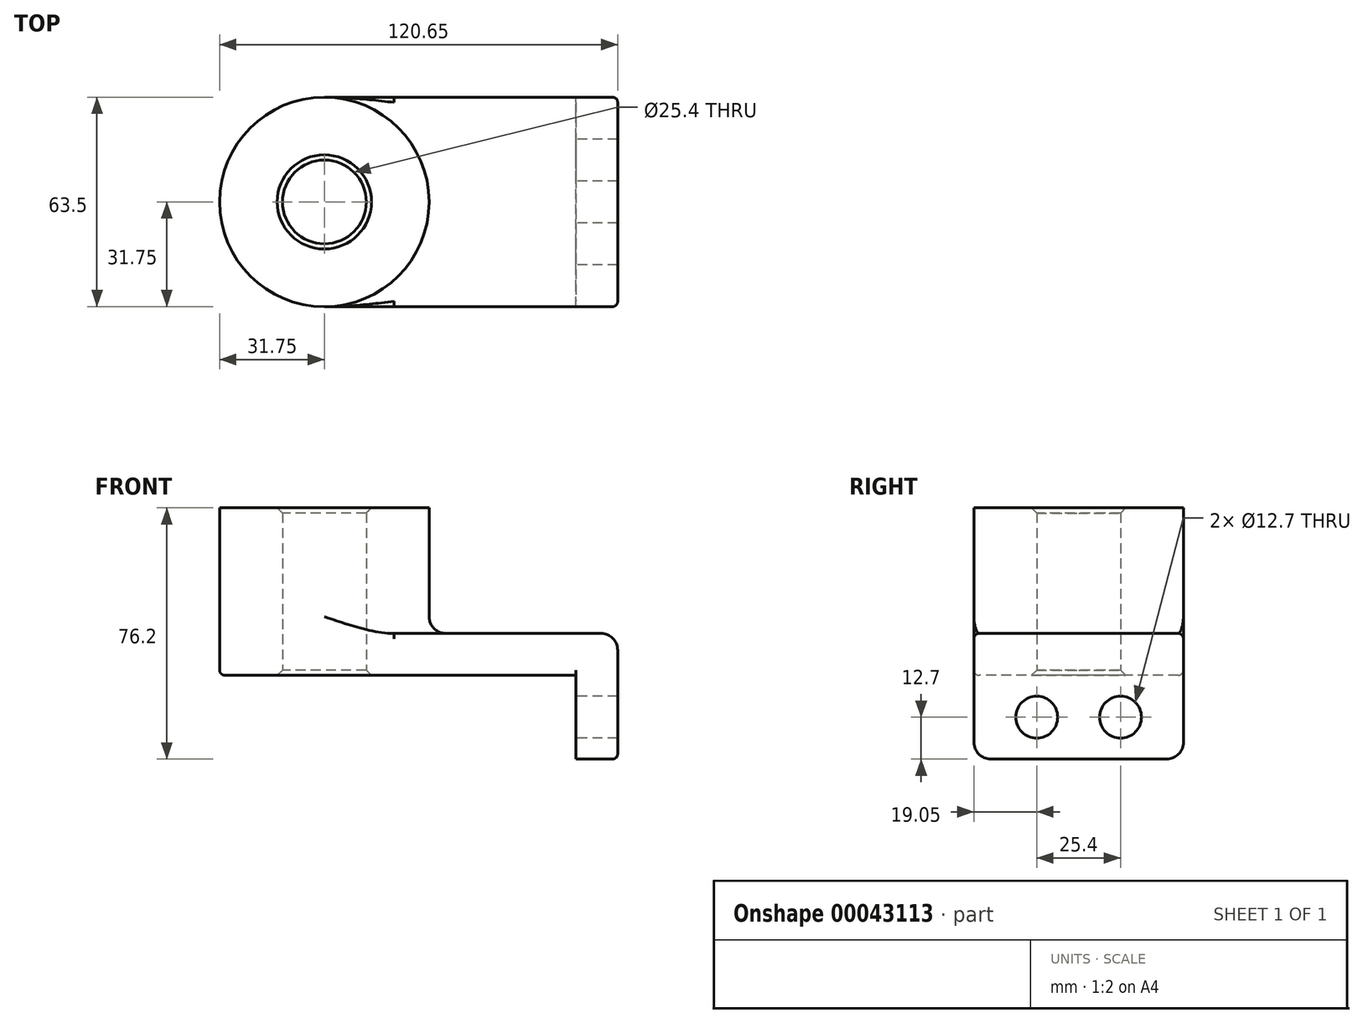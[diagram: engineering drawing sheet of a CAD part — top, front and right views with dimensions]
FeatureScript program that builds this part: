
annotation { "Feature Type Name" : "Feature", "Feature Type Description" : "" }
export const myFeature = defineFeature(function(context is Context, id is Id, definition is map)
    precondition{}
    {
        {
            var Q0;
            Q0=qCreatedBy(makeId("Top.planeOp"),FACE);
            var sketch = newSketch(context, id + "F0", { "sketchPlane" : qUnion([Q0])});
            skLineSegment(sketch, "E0.rect.bottom", {"start": v(-38.1, 31.75) * mm, "end": v(38.1, 31.75) * mm});
            skLineSegment(sketch, "E0.rect.top", {"start": v(-38.1, -31.75) * mm, "end": v(38.1, -31.75) * mm});
            skLineSegment(sketch, "E0.rect.left", {"start": v(-38.1, 31.75) * mm, "end": v(-38.1, -31.75) * mm});
            skLineSegment(sketch, "E0.rect.right", {"start": v(38.1, 31.75) * mm, "end": v(38.1, -31.75) * mm});
            skPoint(sketch, "E0.rect.middle", {"position": v(0, 0) * mm});
            skCircle(sketch, "E1", {"center": v(-38.1, 0) * mm, "radius": 31.75 * mm});
            skCircle(sketch, "E2", {"center": v(-38.1, 0) * mm, "radius": 12.7 * mm});
            skSolve(sketch);
        }
        {
            var Q0;
            Q0 = qSketchRegion(id + "F0", true);
            extrude(context, id + "F1", {"entities" : qUnion([Q0]), "depth" : 12.7 * mm});
        }
        {
            var Q0;
            {var subQ0=sQuery(id+"F0.wireOp",EDGE,"E2");var subQ1=sQuery(id+"F0.wireOp",EDGE,"E0.rect.left");var subQ3=makeQuery(id+"F0.imprint","INTERSECT",VERTEX,{"disambiguationData":[OD(0.0)],"derivedFrom":[subQ1,subQ0]});Q0=makeQuery(id+"F0.imprint","IMPRINT",FACE,{"disambiguationData":[TD([[makeQuery(id+"F0.imprint","IMPRINT",EDGE,{"disambiguationData":[TD([[subQ3,-1.0]])],"derivedFrom":subQ0}),-1.0]])]});}
            var Q1;
            {var subQ0=sQuery(id+"F0.wireOp",EDGE,"E2");var subQ1=sQuery(id+"F0.wireOp",EDGE,"E0.rect.left");var subQ3=makeQuery(id+"F0.imprint","INTERSECT",VERTEX,{"disambiguationData":[OD(0.0)],"derivedFrom":[subQ1,subQ0]});Q1=makeQuery(id+"F0.imprint","IMPRINT",FACE,{"disambiguationData":[TD([[makeQuery(id+"F0.imprint","IMPRINT",EDGE,{"disambiguationData":[TD([[subQ3,1.0]])],"derivedFrom":subQ0}),-1.0]])]});}
            extrude(context, id + "F2", {"entities" : qUnion([Q0, Q1]), "operationType" : NewBodyOperationType.ADD, "depth" : 50.8 * mm});
        }
        {
            var Q0;
            Q0=makeQuery(id+"F1.opExtrude","SWEPT_FACE",FACE,{"disambiguationData":[OSD([sQuery(id+"F0.wireOp",EDGE,"E0.rect.right")])]});
            var sketch = newSketch(context, id + "F3", { "sketchPlane" : qUnion([Q0])});
            skLineSegment(sketch, "E3.bottom", {"start": v(-31.75, 12.7) * mm, "end": v(31.75, 12.7) * mm});
            skLineSegment(sketch, "E3.top", {"start": v(-31.75, -25.4) * mm, "end": v(31.75, -25.4) * mm});
            skLineSegment(sketch, "E3.left", {"start": v(-31.75, 12.7) * mm, "end": v(-31.75, -25.4) * mm});
            skLineSegment(sketch, "E3.right", {"start": v(31.75, 12.7) * mm, "end": v(31.75, -25.4) * mm});
            skCircle(sketch, "E4", {"center": v(-12.7, -12.7) * mm, "radius": 6.35 * mm});
            skLineSegment(sketch, "E5", {"start": v(0, 0) * mm, "end": v(0, -25.4) * mm, "construction": true});
            skCircle(sketch, "E6.MirrorC", {"center": v(12.7, -12.7) * mm, "radius": 6.35 * mm});
            skSolve(sketch);
        }
        {
            var Q0;
            Q0 = qSketchRegion(id + "F3", true);
            extrude(context, id + "F4", {"entities" : qUnion([Q0]), "operationType" : NewBodyOperationType.ADD, "depth" : 12.7 * mm});
        }
        {
            var Q0;
            {var subQ0=sQuery(id+"F0.wireOp",EDGE,"E1");Q0=makeQuery(id+"F2.boolean.opBoolean","INTERSECT",EDGE,{"derivedFrom":[makeQuery(id+"F1.opExtrude","CAP_FACE",FACE,{"disambiguationData":[OSD([sQuery(id+"F0.wireOp",EDGE,"E0.rect.bottom"),sQuery(id+"F0.wireOp",EDGE,"E0.rect.top"),sQuery(id+"F0.wireOp",EDGE,"E0.rect.right"),subQ0,sQuery(id+"F0.wireOp",EDGE,"E2")])],"isStart":false}),makeQuery(id+"F2.opExtrude","SWEPT_FACE",FACE,{"disambiguationData":[OSD([subQ0])]})]});}
            var Q1;
            Q1=makeQuery(id+"F4.opExtrude","CAP_EDGE",EDGE,{"disambiguationData":[OSD([sQuery(id+"F3.wireOp",EDGE,"E3.bottom")])],"isStart":false});
            var Q2;
            Q2=makeQuery(id+"F4.opExtrude","SWEPT_EDGE",EDGE,{"disambiguationData":[OSD([sQuery(id+"F3.wireOp",EDGE,"E3.top"),sQuery(id+"F3.wireOp",EDGE,"E3.left")])]});
            var Q3;
            Q3=makeQuery(id+"F4.opExtrude","SWEPT_EDGE",EDGE,{"disambiguationData":[OSD([sQuery(id+"F3.wireOp",EDGE,"E3.top"),sQuery(id+"F3.wireOp",EDGE,"E3.right")])]});
            fillet(context, id + "F5", {"entities" : qUnion([Q0, Q1, Q2, Q3]), "radius" : 5.08 * mm, "tangentPropagation" : true, "allowEdgeOverflow" : false});
        }
        {
            var Q0;
            Q0=makeQuery(id+"F4.boolean.opBoolean","MERGE",EDGE,{"derivedFrom":[makeQuery(id+"F1.opExtrude","CAP_EDGE",EDGE,{"disambiguationData":[OSD([sQuery(id+"F0.wireOp",EDGE,"E0.rect.top")])],"isStart":false}),makeQuery(id+"F4.opExtrude","SWEPT_EDGE",EDGE,{"disambiguationData":[OSD([sQuery(id+"F3.wireOp",EDGE,"E3.bottom"),sQuery(id+"F3.wireOp",EDGE,"E3.left")])]})]});
            var Q1;
            Q1=makeQuery(id+"F1.opExtrude","CAP_EDGE",EDGE,{"disambiguationData":[OSD([sQuery(id+"F0.wireOp",EDGE,"E0.rect.top")])],"isStart":true});
            var Q2;
            Q2=makeQuery(id+"F1.opExtrude","CAP_EDGE",EDGE,{"disambiguationData":[OSD([sQuery(id+"F0.wireOp",EDGE,"E0.rect.right")])],"isStart":true});
            fillet(context, id + "F6", {"entities" : qUnion([Q0, Q1, Q2]), "radius" : 1.59 * mm, "tangentPropagation" : true, "allowEdgeOverflow" : false});
        }
        {
            var Q0;
            {var subQ0=sQuery(id+"F0.wireOp",EDGE,"E2");Q0=makeQuery(id+"F2.boolean.opBoolean","MERGE",FACE,{"derivedFrom":[makeQuery(id+"F1.opExtrude","SWEPT_FACE",FACE,{"disambiguationData":[OSD([subQ0])]}),makeQuery(id+"F2.opExtrude","SWEPT_FACE",FACE,{"disambiguationData":[OSD([subQ0])]})]});}
            chamfer(context, id + "F7", {"entities" : qUnion([Q0]), "width" : 1.59 * mm, "tangentPropagation" : true});
        }
    });
